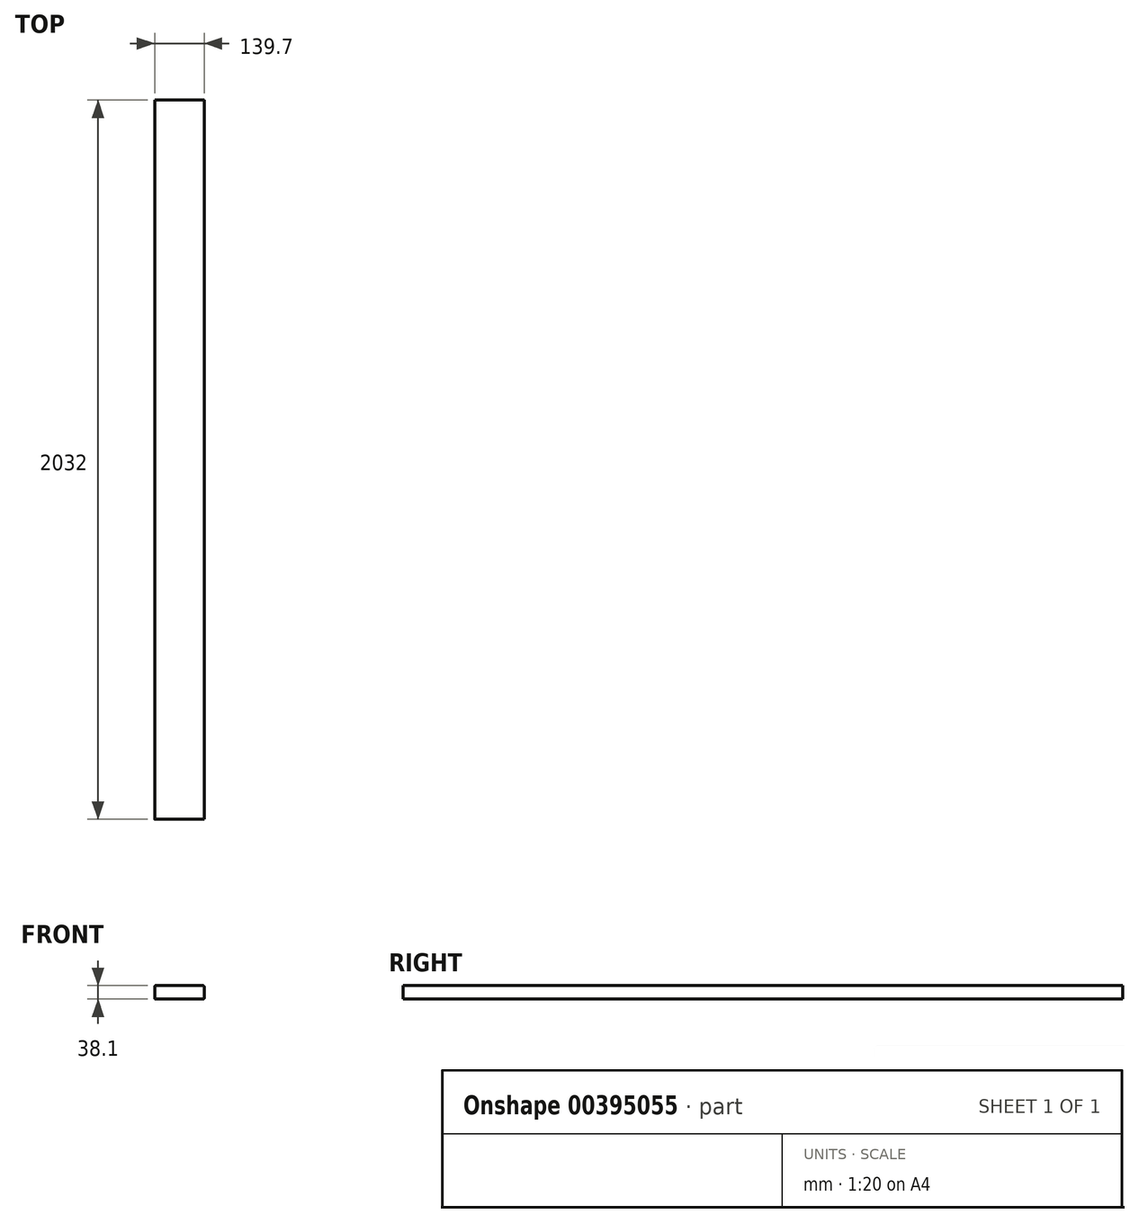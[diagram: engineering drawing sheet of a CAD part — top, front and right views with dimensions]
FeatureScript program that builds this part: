
annotation { "Feature Type Name" : "Feature", "Feature Type Description" : "" }
export const myFeature = defineFeature(function(context is Context, id is Id, definition is map)
    precondition{}
    {
        {
            var Q0;
            Q0=qCreatedBy(makeId("Front.planeOp"),FACE);
            var sketch = newSketch(context, id + "F0", { "sketchPlane" : qUnion([Q0])});
            skLineSegment(sketch, "E0.bottom", {"start": v(3.18, 0) * mm, "end": v(136.52, 0) * mm});
            skLineSegment(sketch, "E0.top", {"start": v(3.17, 38.1) * mm, "end": v(136.53, 38.1) * mm});
            skLineSegment(sketch, "E0.left", {"start": v(0, 3.18) * mm, "end": v(0, 34.93) * mm});
            skLineSegment(sketch, "E0.right", {"start": v(139.7, 3.18) * mm, "end": v(139.7, 34.93) * mm});
            skPoint(sketch, "E1.visualSharp", {"position": v(0, 38.1) * mm});
            skArc(sketch, "E1.filletArc", {"start": v(3.17, 38.1) * mm, "mid": v(0.93, 37.17) * mm, "end": v(0, 34.93) * mm});
            skPoint(sketch, "E2.visualSharp", {"position": v(0, 0) * mm});
            skArc(sketch, "E2.filletArc", {"start": v(0, 3.18) * mm, "mid": v(0.93, 0.93) * mm, "end": v(3.18, 0) * mm});
            skPoint(sketch, "E3.visualSharp", {"position": v(139.7, 0) * mm});
            skArc(sketch, "E3.filletArc", {"start": v(136.52, 0) * mm, "mid": v(138.77, 0.93) * mm, "end": v(139.7, 3.18) * mm});
            skPoint(sketch, "E4.visualSharp", {"position": v(139.7, 38.1) * mm});
            skArc(sketch, "E4.filletArc", {"start": v(139.7, 34.93) * mm, "mid": v(138.77, 37.17) * mm, "end": v(136.53, 38.1) * mm});
            skSolve(sketch);
        }
        {
            var Q0;
            Q0=qSketchRegion(id+"F0",true);
            extrude(context, id + "F1", {"entities" : qUnion([Q0]), "depth" : 2032 * mm});
        }
    });
